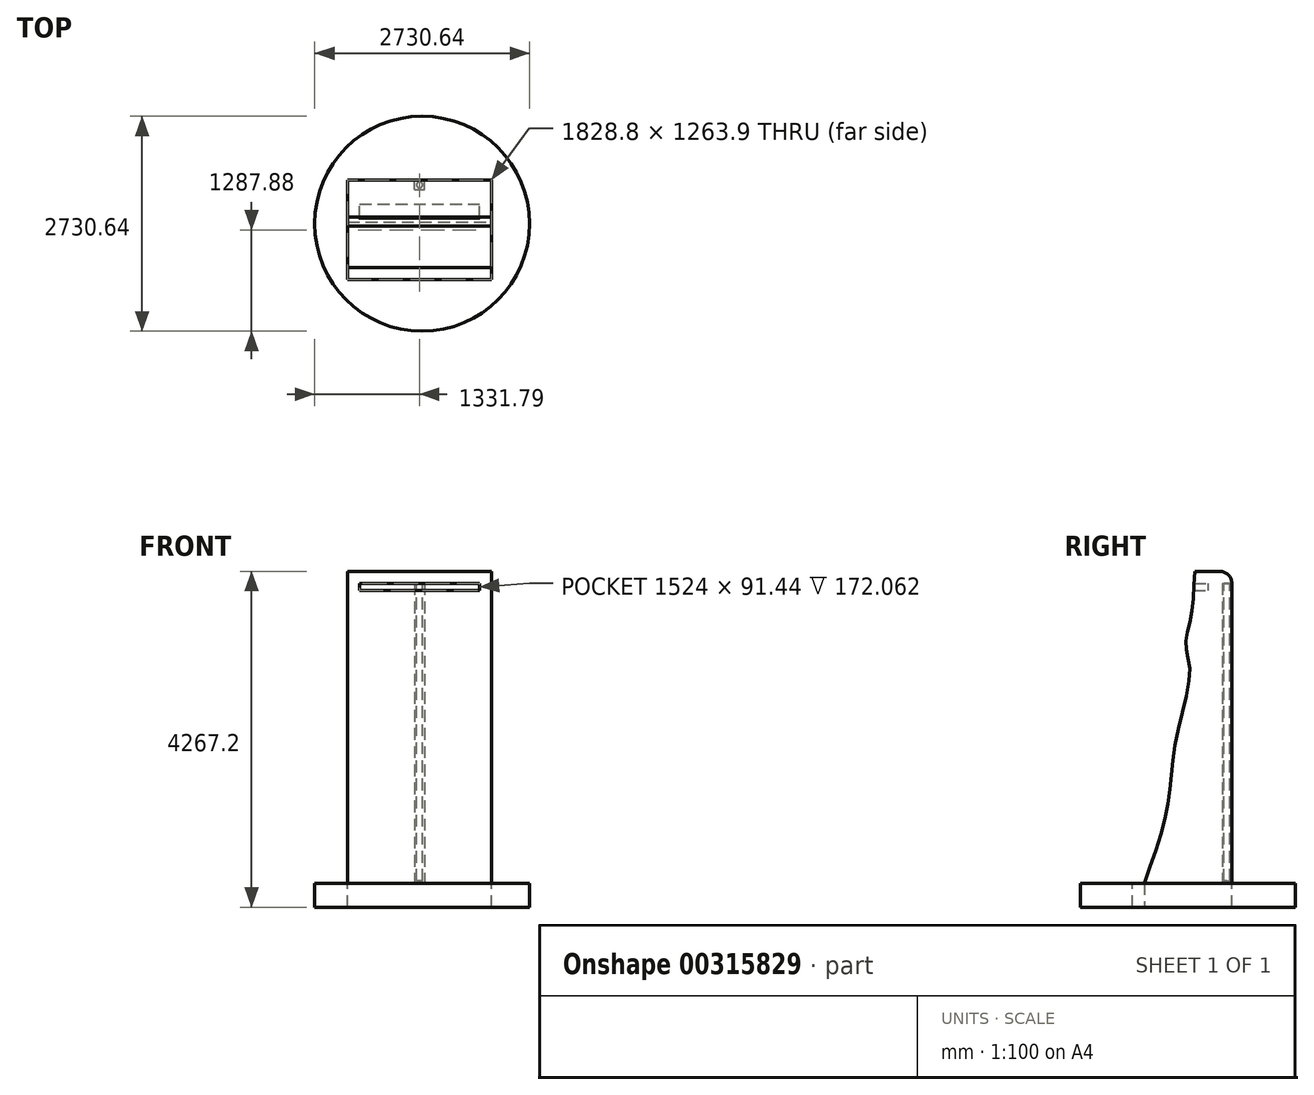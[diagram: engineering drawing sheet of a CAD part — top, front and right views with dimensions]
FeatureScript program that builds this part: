
annotation { "Feature Type Name" : "Feature", "Feature Type Description" : "" }
export const myFeature = defineFeature(function(context is Context, id is Id, definition is map)
    precondition{}
    {
        {
            var Q0;
            Q0=qCreatedBy(makeId("Top.planeOp"),FACE);
            var sketch = newSketch(context, id + "F0", { "sketchPlane" : qUnion([Q0])});
            skLineSegment(sketch, "E0.bottom", {"start": v(-947.94, 1335.97) * mm, "end": v(880.86, 1335.97) * mm});
            skLineSegment(sketch, "E0.top", {"start": v(-947.94, -492.83) * mm, "end": v(880.86, -492.83) * mm});
            skLineSegment(sketch, "E0.left", {"start": v(-947.94, 1335.97) * mm, "end": v(-947.94, -492.83) * mm});
            skLineSegment(sketch, "E0.right", {"start": v(880.86, 1335.97) * mm, "end": v(880.86, -492.83) * mm});
            skSolve(sketch);
        }
        {
            var Q0;
            Q0=makeQuery(id+"F0.imprint","IMPRINT",FACE,{"disambiguationData":[TD([[makeQuery(id+"F0.imprint","IMPRINT",EDGE,{"derivedFrom":sQuery(id+"F0.wireOp",EDGE,"E0.bottom")}),-1.0]])]});
            extrude(context, id + "F1", {"entities" : qUnion([Q0]), "depth" : 3962.4 * mm});
        }
        {
            var Q0;
            Q0=makeQuery(id+"F1.opExtrude","SWEPT_FACE",FACE,{"disambiguationData":[OSD([sQuery(id+"F0.wireOp",EDGE,"E0.right")])]});
            var sketch = newSketch(context, id + "F2", { "sketchPlane" : qUnion([Q0])});
            skFitSpline(sketch, "E1", {"points": [v(867.2, 3962.4) * mm, v(810.4, 3347.84) * mm, v(752.1, 3024.57) * mm, v(802.75, 2689) * mm, v(617.46, 1775.1) * mm, v(520.5, 979.15) * mm, v(224.47, 0) * mm], "startDerivative": vector(-207.26, -4060.73) * mm, "endDerivative": vector(-1728.74, -4830.39) * mm});
            skSolve(sketch);
        }
        {
            var Q0;
            {var subQ0=sQuery(id+"F2.wireOp",EDGE,"E1");Q0=makeQuery(id+"F2.imprint","IMPRINT",FACE,{"disambiguationData":[TD([[makeQuery(id+"F2.imprint","IMPRINT",EDGE,{"derivedFrom":subQ0}),-1.0]])]});}
            extrude(context, id + "F3", {"entities" : qUnion([Q0]), "operationType" : NewBodyOperationType.REMOVE, "endBound" : BoundingType.THROUGH_ALL, "oppositeDirection" : true, "depth" : 30.48 * mm});
        }
        {
            var Q0;
            Q0=makeQuery(id+"F1.opExtrude","CAP_FACE",FACE,{"disambiguationData":[OSD([sQuery(id+"F0.wireOp",EDGE,"E0.bottom"),sQuery(id+"F0.wireOp",EDGE,"E0.top"),sQuery(id+"F0.wireOp",EDGE,"E0.left"),sQuery(id+"F0.wireOp",EDGE,"E0.right")])],"isStart":true});
            var sketch = newSketch(context, id + "F4", { "sketchPlane" : qUnion([Q0])});
            skLineSegment(sketch, "E2", {"start": v(880.86, -224.47) * mm, "end": v(880.86, -780.22) * mm});
            skLineSegment(sketch, "E3", {"start": v(880.86, -780.22) * mm, "end": v(0, -781.46) * mm});
            skCircle(sketch, "E4", {"center": v(0, -781.46) * mm, "radius": 1365.32 * mm});
            skSolve(sketch);
        }
        {
            var Q0;
            {var subQ4=sQuery(id+"F4.wireOp",EDGE,"E2");Q0=makeQuery(id+"F4.imprint","IMPRINT",FACE,{"disambiguationData":[TD([[makeQuery(id+"F4.imprint","IMPRINT",EDGE,{"derivedFrom":subQ4}),-1.0]])]});}
            extrude(context, id + "F5", {"entities" : qUnion([Q0]), "depth" : 304.8 * mm});
        }
        {
            var Q0;
            Q0=makeQuery(id+"F5.opExtrude","CAP_FACE",FACE,{"disambiguationData":[OSD([sQuery(id+"F0.wireOp",EDGE,"E0.bottom"),sQuery(id+"F0.wireOp",EDGE,"E0.left"),sQuery(id+"F0.wireOp",EDGE,"E0.right"),sQuery(id+"F2.wireOp",EDGE,"E1"),sQuery(id+"F4.wireOp",EDGE,"E2"),sQuery(id+"F4.wireOp",EDGE,"E4")])],"isStart":false});
            var sketch = newSketch(context, id + "F6", { "sketchPlane" : qUnion([Q0])});
            skSolve(sketch);
        }
        {
            var Q0;
            Q0=makeQuery(id+"F6.imprint","IMPRINT",FACE,{"disambiguationData":[TD([[makeQuery(id+"F6.imprint","IMPRINT",EDGE,{"derivedFrom":makeQuery(id+"F5.opExtrude","CAP_EDGE",EDGE,{"disambiguationData":[OSD([sQuery(id+"F0.wireOp",EDGE,"E0.bottom")])],"isStart":false})}),1.0]])]});
            var sketch = newSketch(context, id + "F7", { "sketchPlane" : qUnion([Q0])});
            skCircle(sketch, "E5", {"center": v(0, -792.98) * mm, "radius": 1795.33 * mm});
            skSolve(sketch);
        }
        {
            var Q0;
            Q0=makeQuery(id+"F6.imprint","IMPRINT",FACE,{"disambiguationData":[TD([[makeQuery(id+"F6.imprint","IMPRINT",EDGE,{"derivedFrom":makeQuery(id+"F5.opExtrude","CAP_EDGE",EDGE,{"disambiguationData":[OSD([sQuery(id+"F0.wireOp",EDGE,"E0.bottom")])],"isStart":false})}),1.0]])]});
            extrude(context, id + "F8", {"entities" : qUnion([Q0]), "oppositeDirection" : true, "depth" : 304.8 * mm});
        }
        {
            var Q0;
            Q0=makeQuery(id+"F7.imprint","IMPRINT",FACE,{"disambiguationData":[TD([[makeQuery(id+"F7.imprint","IMPRINT",EDGE,{"derivedFrom":sQuery(id+"F7.wireOp",EDGE,"E5")}),1.0]])]});
            extrude(context, id + "F9", {"entities" : qUnion([Q0]), "depth" : 304.8 * mm});
        }
        {
            var Q0;
            Q0=makeQuery(id+"F1.opExtrude","CAP_EDGE",EDGE,{"disambiguationData":[OSD([sQuery(id+"F0.wireOp",EDGE,"E0.bottom")])],"isStart":false});
            fillet(context, id + "F10", {"entities" : qUnion([Q0]), "radius" : 152.4 * mm, "tangentPropagation" : true, "allowEdgeOverflow" : false});
        }
        {
            var Q0;
            Q0=makeQuery(id+"F1.opExtrude","SWEPT_FACE",FACE,{"disambiguationData":[OSD([sQuery(id+"F0.wireOp",EDGE,"E0.bottom")])]});
            var sketch = newSketch(context, id + "F11", { "sketchPlane" : qUnion([Q0])});
            skLineSegment(sketch, "E6", {"start": v(-880.86, 3810) * mm, "end": v(-728.46, 3810) * mm});
            skLineSegment(sketch, "E7", {"start": v(947.94, 3810) * mm, "end": v(795.54, 3810) * mm});
            skLineSegment(sketch, "E8.bottom", {"start": v(-728.46, 3810) * mm, "end": v(795.54, 3810) * mm});
            skLineSegment(sketch, "E8.top", {"start": v(-728.46, 3718.56) * mm, "end": v(795.54, 3718.56) * mm});
            skLineSegment(sketch, "E8.left", {"start": v(-728.46, 3810) * mm, "end": v(-728.46, 3718.56) * mm});
            skLineSegment(sketch, "E8.right", {"start": v(795.54, 3810) * mm, "end": v(795.54, 3718.56) * mm});
            skSolve(sketch);
        }
        {
            var Q0;
            Q0=makeQuery(id+"F11.imprint","IMPRINT",FACE,{"disambiguationData":[TD([[makeQuery(id+"F11.imprint","IMPRINT",EDGE,{"derivedFrom":sQuery(id+"F11.wireOp",EDGE,"E8.bottom")}),1.0]])]});
            extrude(context, id + "F12", {"entities" : qUnion([Q0]), "operationType" : NewBodyOperationType.REMOVE, "endBound" : BoundingType.THROUGH_ALL, "oppositeDirection" : true, "depth" : 30.48 * mm});
        }
        {
            var Q0;
            Q0=makeQuery(id+"F12.boolean.opBoolean","COPY",FACE,{"derivedFrom":makeQuery(id+"F12.opExtrude","SWEPT_FACE",FACE,{"disambiguationData":[OSD([sQuery(id+"F11.wireOp",EDGE,"E8.top")])]})});
            var sketch = newSketch(context, id + "F13", { "sketchPlane" : qUnion([Q0])});
            skLineSegment(sketch, "E9.bottom", {"start": v(-795.54, 1335.97) * mm, "end": v(728.46, 1335.97) * mm});
            skLineSegment(sketch, "E9.top", {"start": v(-795.54, 1031.17) * mm, "end": v(728.46, 1031.17) * mm});
            skLineSegment(sketch, "E9.left", {"start": v(-795.54, 1335.97) * mm, "end": v(-795.54, 1031.17) * mm});
            skLineSegment(sketch, "E9.right", {"start": v(728.46, 1335.97) * mm, "end": v(728.46, 1031.17) * mm});
            skSolve(sketch);
        }
        {
            var Q0;
            Q0=makeQuery(id+"F13.imprint","IMPRINT",FACE,{"disambiguationData":[TD([[makeQuery(id+"F13.imprint","IMPRINT",EDGE,{"derivedFrom":sQuery(id+"F13.wireOp",EDGE,"E9.bottom")}),1.0]])]});
            extrude(context, id + "F14", {"entities" : qUnion([Q0]), "operationType" : NewBodyOperationType.ADD, "depth" : 91.44 * mm});
        }
        {
            var Q0;
            Q0=makeQuery(id+"F14.boolean.opBoolean","MERGE",FACE,{"derivedFrom":[makeQuery(id+"F1.opExtrude","SWEPT_FACE",FACE,{"disambiguationData":[OSD([sQuery(id+"F0.wireOp",EDGE,"E0.bottom")])]}),makeQuery(id+"F14.opExtrude","SWEPT_FACE",FACE,{"disambiguationData":[OSD([sQuery(id+"F13.wireOp",EDGE,"E9.bottom")])]})]});
            var sketch = newSketch(context, id + "F15", { "sketchPlane" : qUnion([Q0])});
            skLineSegment(sketch, "E10", {"start": v(-880.86, 3810) * mm, "end": v(-27.42, 3810) * mm});
            skLineSegment(sketch, "E11", {"start": v(947.94, 3810) * mm, "end": v(94.5, 3810) * mm});
            skLineSegment(sketch, "E12.bottom", {"start": v(-27.42, 3810) * mm, "end": v(94.5, 3810) * mm});
            skLineSegment(sketch, "E12.top", {"start": v(-27.42, 0) * mm, "end": v(94.5, 0) * mm});
            skLineSegment(sketch, "E12.left", {"start": v(-27.42, 3810) * mm, "end": v(-27.42, 0) * mm});
            skLineSegment(sketch, "E12.right", {"start": v(94.5, 3810) * mm, "end": v(94.5, 0) * mm});
            skSolve(sketch);
        }
        {
            var Q0;
            Q0=makeQuery(id+"F15.imprint","IMPRINT",FACE,{"disambiguationData":[TD([[makeQuery(id+"F15.imprint","IMPRINT",EDGE,{"derivedFrom":sQuery(id+"F15.wireOp",EDGE,"E12.bottom")}),1.0]])]});
            extrude(context, id + "F16", {"entities" : qUnion([Q0]), "operationType" : NewBodyOperationType.REMOVE, "oppositeDirection" : true, "depth" : 121.92 * mm});
        }
        {
            var Q0;
            Q0=makeQuery(id+"F16.boolean.opBoolean","COPY",FACE,{"derivedFrom":makeQuery(id+"F16.opExtrude","SWEPT_FACE",FACE,{"disambiguationData":[OSD([sQuery(id+"F15.wireOp",EDGE,"E12.bottom")])]})});
            var sketch = newSketch(context, id + "F17", { "sketchPlane" : qUnion([Q0])});
            skCircle(sketch, "E13", {"center": v(-33.54, -1275) * mm, "radius": 38.1 * mm});
            skPoint(sketch, "E13.centerSnap0", {"position": v(-94.5, -1275) * mm});
            skPoint(sketch, "E13.centerSnap1", {"position": v(-33.54, -1214.05) * mm});
            skSolve(sketch);
        }
        {
            var Q0;
            Q0=makeQuery(id+"F17.imprint","IMPRINT",FACE,{"disambiguationData":[TD([[makeQuery(id+"F17.imprint","IMPRINT",EDGE,{"derivedFrom":sQuery(id+"F17.wireOp",EDGE,"E13")}),1.0]])]});
            extrude(context, id + "F18", {"entities" : qUnion([Q0]), "operationType" : NewBodyOperationType.ADD, "depth" : 3779.52 * mm});
        }
        {
            var Q0;
            Q0=makeQuery(id+"F9.opExtrude","SWEPT_BODY",BODY,{"disambiguationData":[OSD([sQuery(id+"F0.wireOp",EDGE,"E0.bottom"),sQuery(id+"F0.wireOp",EDGE,"E0.left"),sQuery(id+"F0.wireOp",EDGE,"E0.right"),sQuery(id+"F2.wireOp",EDGE,"E1"),sQuery(id+"F4.wireOp",EDGE,"E2"),sQuery(id+"F7.wireOp",EDGE,"E5")])]});
            deleteBodies(context, id + "F19", {"entities" : qUnion([Q0])});
        }
        {
            var Q0;
            Q0=makeQuery(id+"F5.opExtrude","CAP_FACE",FACE,{"disambiguationData":[OSD([sQuery(id+"F0.wireOp",EDGE,"E0.bottom"),sQuery(id+"F0.wireOp",EDGE,"E0.left"),sQuery(id+"F0.wireOp",EDGE,"E0.right"),sQuery(id+"F2.wireOp",EDGE,"E1"),sQuery(id+"F4.wireOp",EDGE,"E2"),sQuery(id+"F4.wireOp",EDGE,"E4")])],"isStart":true});
            var sketch = newSketch(context, id + "F20", { "sketchPlane" : qUnion([Q0])});
            skLineSegment(sketch, "E14.bottom", {"start": v(-947.94, 224.47) * mm, "end": v(880.86, 224.47) * mm});
            skLineSegment(sketch, "E14.top", {"start": v(-947.94, 72.07) * mm, "end": v(880.86, 72.07) * mm});
            skLineSegment(sketch, "E14.left", {"start": v(-947.94, 224.47) * mm, "end": v(-947.94, 72.07) * mm});
            skLineSegment(sketch, "E14.right", {"start": v(880.86, 224.47) * mm, "end": v(880.86, 72.07) * mm});
            skSolve(sketch);
        }
        {
            var Q0;
            Q0=makeQuery(id+"F20.imprint","IMPRINT",FACE,{"disambiguationData":[TD([[makeQuery(id+"F20.imprint","IMPRINT",EDGE,{"derivedFrom":sQuery(id+"F20.wireOp",EDGE,"E14.bottom")}),-1.0]])]});
            extrude(context, id + "F21", {"entities" : qUnion([Q0]), "operationType" : NewBodyOperationType.REMOVE, "endBound" : BoundingType.THROUGH_ALL, "oppositeDirection" : true, "depth" : 30.48 * mm});
        }
    });
